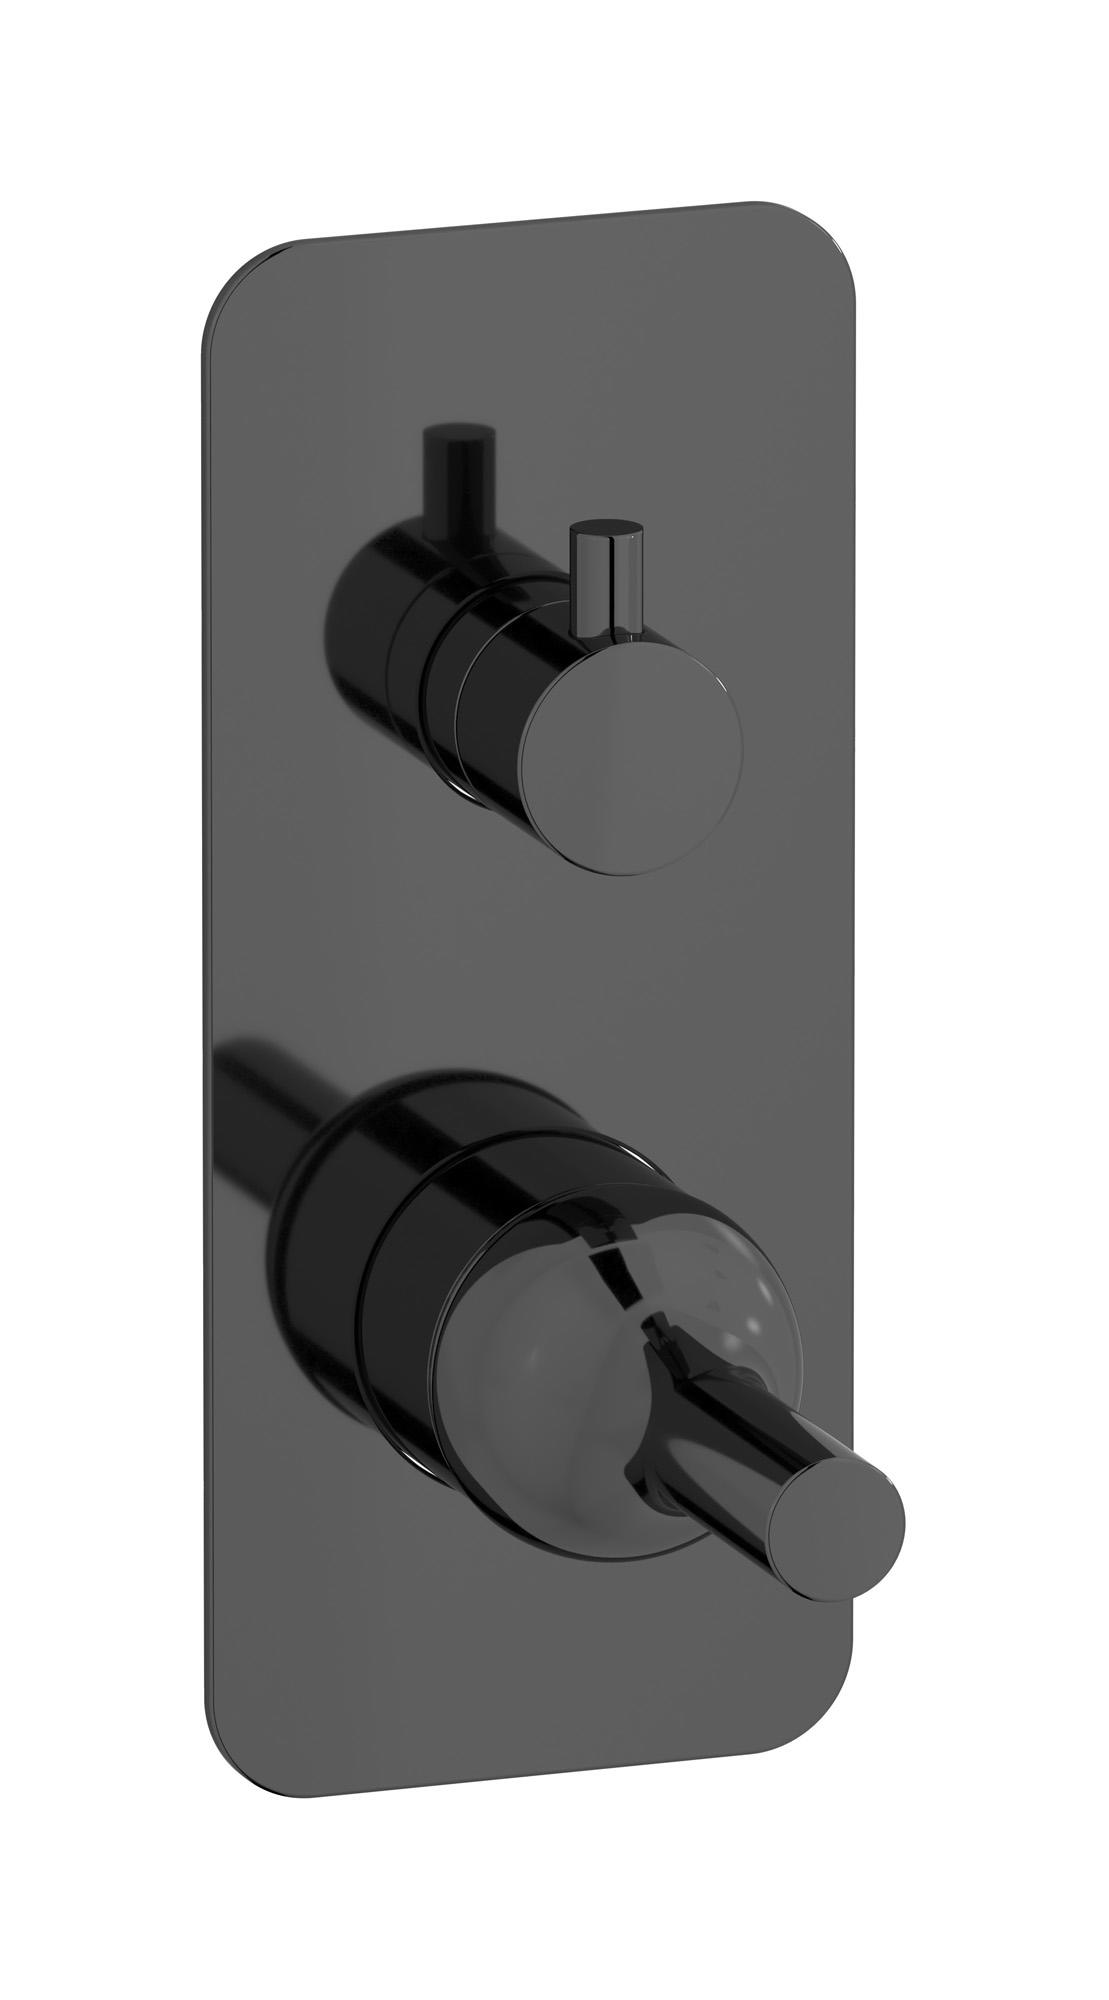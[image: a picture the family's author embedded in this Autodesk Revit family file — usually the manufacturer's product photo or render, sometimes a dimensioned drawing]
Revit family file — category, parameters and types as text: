
# Revit family: BI312
name_source: partatom
category: Apparecchi idraulici
units: mm (PartAtom-declared; Revit-internal decimal feet)

## family parameters
Basato su piano di lavoro = No
Condiviso = No
Mantieni orientamento annotazione = No
Numero OmniClass = 23.45.55.17
Punto di calcolo locali = No
Quota connettore circolare = Usa diametro
Sempre verticale = Sì
Taglio con vuoti quando caricato = No
Tipo di parte = Normale
Titolo OmniClass = Mixing Faucets

## types (4) — shared parameters
Cold water inlet = 10 mm  [stored 0.0328084 ft]
Commenti sul tipo = Wall mixer
Connessione CW = No
Connessione HW = No
Connessione di scarico = No
Connessione di ventilazione = No
Descrizione = Exposed parts for manual wall mixer with three ways diverter
Hot water inlet = 10 mm  [stored 0.0328084 ft]
Produttore = IB Rubinetterie S.p.A.
URL = https://www.weareib.it
zero-valued in all types: Prospetto di default

## per-type parameters (varying)
| type | Finishes surface | Immagine tipo | Modello |
| Chrome | IB_Chrome | BI312CC.jpg | BI312CC |
| Brushed nickel | IB_Brushed nickel | BI312SS.jpg | BI312SS |
| Matt black | IB_matt black | BI312NP.jpg | BI312NP |
| Matt white | IB_matt white | BI312BO.jpg | BI312BO |

note: [stored X ft] marks values corroborated as IEEE doubles in the binary element streams (Revit-internal decimal feet)
